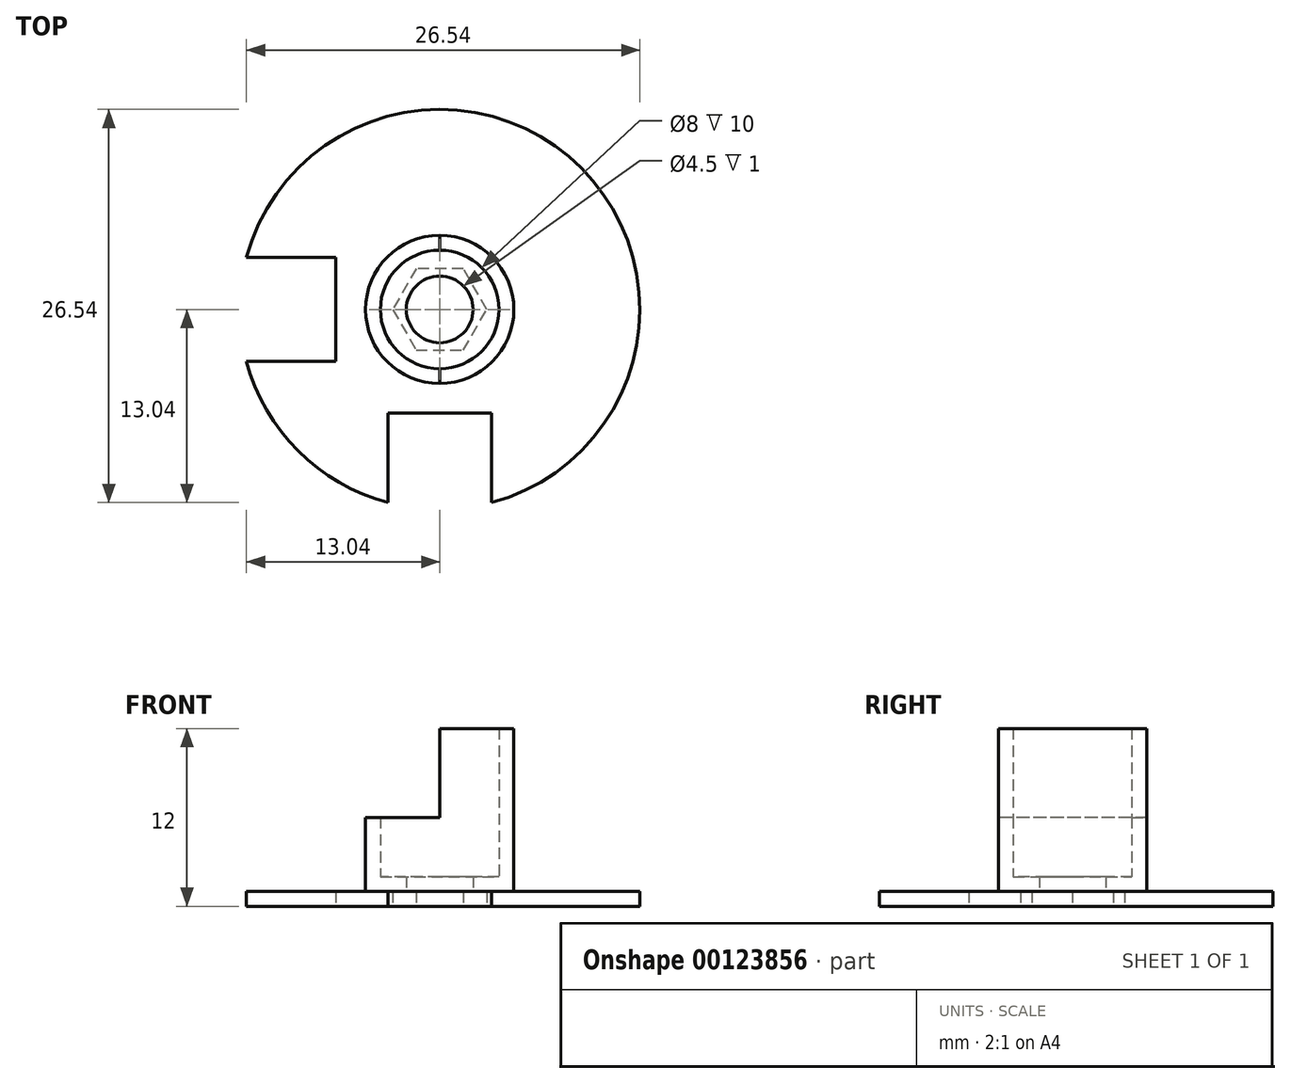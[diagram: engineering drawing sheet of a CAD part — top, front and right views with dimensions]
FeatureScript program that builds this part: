
annotation { "Feature Type Name" : "Feature", "Feature Type Description" : "" }
export const myFeature = defineFeature(function(context is Context, id is Id, definition is map)
    precondition{}
    {
        {
            var Q0;
            Q0=qCreatedBy(makeId("Top.planeOp"),FACE);
            var sketch = newSketch(context, id + "F0", { "sketchPlane" : qUnion([Q0])});
            skCircle(sketch, "E0", {"center": v(0, 0) * mm, "radius": 13.5 * mm});
            skSolve(sketch);
        }
        {
            var Q0;
            Q0 = qSketchRegion(id + "F0", true);
            extrude(context, id + "F1", {"entities" : qUnion([Q0]), "depth" : 1 * mm});
        }
        {
            var Q0;
            Q0=makeQuery(id+"F1.opExtrude","CAP_FACE",FACE,{"disambiguationData":[OSD([sQuery(id+"F0.wireOp",EDGE,"E0")])],"isStart":false});
            var sketch = newSketch(context, id + "F2", { "sketchPlane" : qUnion([Q0])});
            skCircle(sketch, "E1", {"center": v(0, 0) * mm, "radius": 5 * mm});
            skCircle(sketch, "E2", {"center": v(0, 0) * mm, "radius": 4 * mm});
            skSolve(sketch);
        }
        {
            var Q0;
            Q0 = qSketchRegion(id + "F2", true);
            extrude(context, id + "F3", {"entities" : qUnion([Q0]), "operationType" : NewBodyOperationType.ADD, "depth" : 5 * mm});
        }
        {
            var Q0;
            Q0=makeQuery(id+"F3.opExtrude","CAP_FACE",FACE,{"disambiguationData":[OSD([sQuery(id+"F2.wireOp",EDGE,"E1"),sQuery(id+"F2.wireOp",EDGE,"E2")])],"isStart":false});
            var sketch = newSketch(context, id + "F4", { "sketchPlane" : qUnion([Q0])});
            skArc(sketch, "E3.0", {"start": v(0, -5) * mm, "mid": v(5, 0) * mm, "end": v(0, 5) * mm});
            skArc(sketch, "E4.0", {"start": v(0, -4) * mm, "mid": v(4, 0) * mm, "end": v(0, 4) * mm});
            skLineSegment(sketch, "E5", {"start": v(0, 4) * mm, "end": v(0, 5) * mm});
            skLineSegment(sketch, "E6", {"start": v(0, -4) * mm, "end": v(0, -5) * mm});
            skSolve(sketch);
        }
        {
            var Q0;
            Q0 = qSketchRegion(id + "F4", true);
            extrude(context, id + "F5", {"entities" : qUnion([Q0]), "operationType" : NewBodyOperationType.ADD, "depth" : 6 * mm});
        }
        {
            var Q0;
            Q0=makeQuery(id+"F1.opExtrude","CAP_FACE",FACE,{"disambiguationData":[OSD([sQuery(id+"F0.wireOp",EDGE,"E0")])],"isStart":true});
            var sketch = newSketch(context, id + "F6", { "sketchPlane" : qUnion([Q0])});
            skCircle(sketch, "E7.cCircle", {"center": v(0, 0) * mm, "radius": 2.75 * mm, "construction": true});
            skLineSegment(sketch, "E7.0", {"start": v(1.59, 2.75) * mm, "end": v(3.18, 0) * mm});
            skLineSegment(sketch, "E7.1", {"start": v(3.18, 0) * mm, "end": v(1.59, -2.75) * mm});
            skLineSegment(sketch, "E7.2", {"start": v(1.59, -2.75) * mm, "end": v(-1.59, -2.75) * mm});
            skLineSegment(sketch, "E7.3", {"start": v(-1.59, -2.75) * mm, "end": v(-3.18, 0) * mm});
            skLineSegment(sketch, "E7.4", {"start": v(-3.18, 0) * mm, "end": v(-1.59, 2.75) * mm});
            skLineSegment(sketch, "E7.5", {"start": v(-1.59, 2.75) * mm, "end": v(1.59, 2.75) * mm});
            skPoint(sketch, "E7.0.midPoint", {"position": v(2.38, 1.37) * mm});
            skArc(sketch, "E8.0", {"start": v(-13.04, 3.5) * mm, "mid": v(-13.5, 0) * mm, "end": v(-13.04, -3.5) * mm});
            skLineSegment(sketch, "E9", {"start": v(0, 0) * mm, "end": v(0, 16.4) * mm, "construction": true});
            skPoint(sketch, "E9.endSnap0", {"position": v(0, 2.75) * mm});
            skLineSegment(sketch, "E10", {"start": v(0, 0) * mm, "end": v(-16, 0) * mm, "construction": true});
            skLineSegment(sketch, "E11", {"start": v(0, 7) * mm, "end": v(-3.5, 7) * mm});
            skLineSegment(sketch, "E12", {"start": v(-3.5, 7) * mm, "end": v(-3.5, 13.04) * mm});
            skLineSegment(sketch, "E13.MirrorCS", {"start": v(3.5, 7) * mm, "end": v(3.5, 13.04) * mm});
            skLineSegment(sketch, "E14.MirrorCS", {"start": v(0, 7) * mm, "end": v(3.5, 7) * mm});
            skLineSegment(sketch, "E15", {"start": v(-7, 0) * mm, "end": v(-7, 3.5) * mm});
            skLineSegment(sketch, "E16", {"start": v(-7, 3.5) * mm, "end": v(-13.04, 3.5) * mm});
            skLineSegment(sketch, "E17.MirrorCS", {"start": v(-7, 0) * mm, "end": v(-7, -3.5) * mm});
            skLineSegment(sketch, "E18.MirrorCS", {"start": v(-7, -3.5) * mm, "end": v(-13.04, -3.5) * mm});
            skArc(sketch, "E19.trimOffspring", {"start": v(3.5, 13.04) * mm, "mid": v(0, 13.5) * mm, "end": v(-3.5, 13.04) * mm});
            skSolve(sketch);
        }
        {
            var Q0;
            Q0=makeQuery(id+"F6.imprint","IMPRINT",FACE,{"disambiguationData":[TD([[makeQuery(id+"F6.imprint","IMPRINT",EDGE,{"derivedFrom":sQuery(id+"F6.wireOp",EDGE,"E7.0")}),-1.0]])]});
            var Q1;
            Q1=makeQuery(id+"F6.imprint","IMPRINT",FACE,{"disambiguationData":[TD([[makeQuery(id+"F6.imprint","IMPRINT",EDGE,{"derivedFrom":sQuery(id+"F6.wireOp",EDGE,"E11")}),-1.0]])]});
            var Q2;
            Q2=makeQuery(id+"F6.imprint","IMPRINT",FACE,{"disambiguationData":[TD([[makeQuery(id+"F6.imprint","IMPRINT",EDGE,{"derivedFrom":sQuery(id+"F6.wireOp",EDGE,"E8.0")}),-1.0]])]});
            extrude(context, id + "F7", {"entities" : qUnion([Q0, Q1, Q2]), "operationType" : NewBodyOperationType.REMOVE, "endBound" : BoundingType.THROUGH_ALL, "oppositeDirection" : true, "depth" : 25 * mm});
        }
        {
            var Q0;
            Q0=makeQuery(id+"F3.boolean.opBoolean","SPLIT",FACE,{"disambiguationData":[TD([makeQuery(id+"F3.opExtrude","SWEPT_FACE",FACE,{"disambiguationData":[OSD([sQuery(id+"F2.wireOp",EDGE,"E2")])]})])],"derivedFrom":makeQuery(id+"F1.opExtrude","CAP_FACE",FACE,{"disambiguationData":[OSD([sQuery(id+"F0.wireOp",EDGE,"E0")])],"isStart":false})});
            var sketch = newSketch(context, id + "F8", { "sketchPlane" : qUnion([Q0])});
            skCircle(sketch, "E20", {"center": v(0, 0) * mm, "radius": 2.25 * mm});
            skCircle(sketch, "E21.0", {"center": v(0, 0) * mm, "radius": 4 * mm});
            skSolve(sketch);
        }
        {
            var Q0;
            Q0 = qSketchRegion(id + "F8", true);
            extrude(context, id + "F9", {"entities" : qUnion([Q0]), "operationType" : NewBodyOperationType.ADD, "depth" : 1 * mm});
        }
    });
